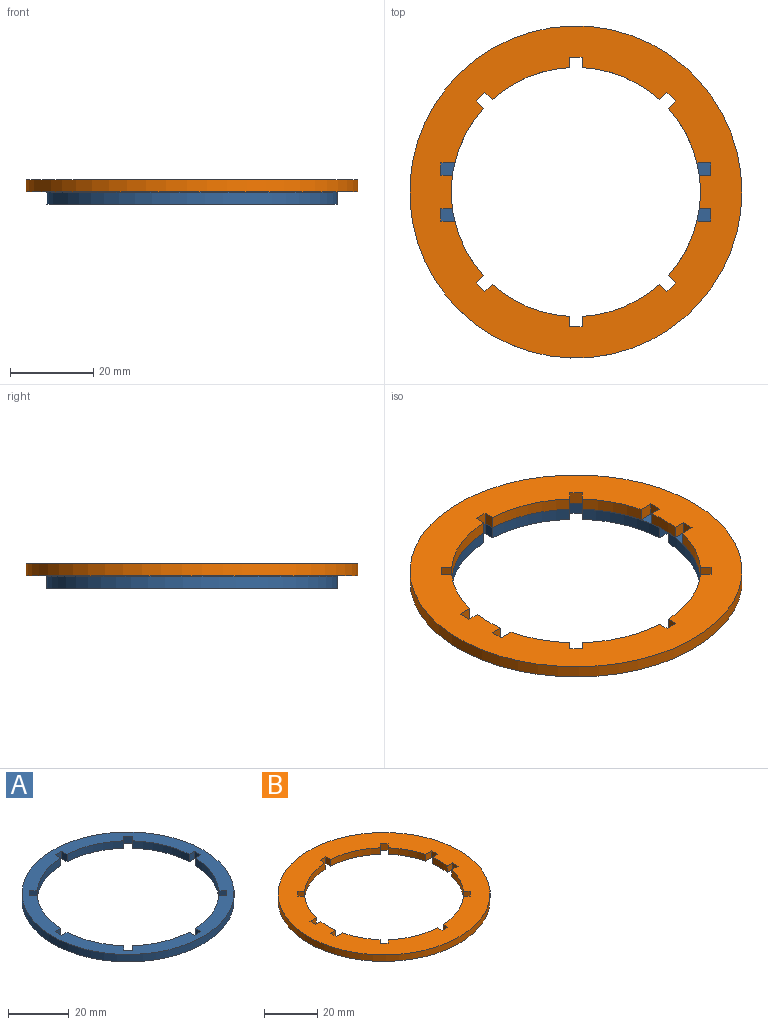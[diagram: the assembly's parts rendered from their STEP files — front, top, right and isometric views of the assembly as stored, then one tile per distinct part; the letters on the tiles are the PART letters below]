
ASSEMBLY  parts=2 mates=1
PART A: 35 faces, bbox 70x70x3 mm
  f0: cylinder r=30mm len=18.63mm, axis (0,0,-1), area 61.7mm2, adj f1,f31,f33,f34
  f1: plane 3x1.79mm, normal (-0.71,0.71,0), area 7.6mm2, adj f0,f2,f33,f34
  f2: plane 3x2.12mm, normal (0.71,0.71,0), area 9mm2, adj f1,f3,f33,f34
  f3: plane 3x1.79mm, normal (0.71,-0.71,0), area 7.6mm2, adj f2,f4,f33,f34
  f4: cylinder r=30mm len=18.63mm, axis (0,0,-1), area 61.7mm2, adj f3,f5,f33,f34
  f5: plane 3x2.54mm, normal (0,1,0), area 7.6mm2, adj f4,f6,f33,f34
  f6: plane 3x3mm, normal (1,0,0), area 9mm2, adj f5,f7,f33,f34
  f7: plane 3x2.54mm, normal (0,-1,0), area 7.6mm2, adj f6,f8,f33,f34
  f8: cylinder r=30mm len=18.63mm, axis (0,0,-1), area 61.7mm2, adj f7,f9,f33,f34
  f9: plane 3x1.79mm, normal (0.71,0.71,0), area 7.6mm2, adj f8,f10,f33,f34
  f10: plane 3x2.12mm, normal (0.71,-0.71,0), area 9mm2, adj f9,f11,f33,f34
  f11: plane 3x1.79mm, normal (-0.71,-0.71,0), area 7.6mm2, adj f10,f12,f33,f34
  f12: cylinder r=30mm len=18.63mm, axis (0,0,-1), area 61.7mm2, adj f11,f13,f33,f34
  f13: plane 3x2.54mm, normal (1,0,0), area 7.6mm2, adj f12,f14,f33,f34
  f14: plane 3x3mm, normal (0,-1,0), area 9mm2, adj f13,f15,f33,f34
  f15: plane 3x2.54mm, normal (-1,0,0), area 7.6mm2, adj f14,f16,f33,f34
  f16: cylinder r=30mm len=18.63mm, axis (0,0,-1), area 61.7mm2, adj f15,f17,f33,f34
  f17: plane 3x1.79mm, normal (0.71,-0.71,0), area 7.6mm2, adj f16,f18,f33,f34
  f18: plane 3x2.12mm, normal (-0.71,-0.71,0), area 9mm2, adj f17,f19,f33,f34
  f19: plane 3x1.79mm, normal (-0.71,0.71,0), area 7.6mm2, adj f18,f20,f33,f34
  f20: cylinder r=30mm len=18.63mm, axis (0,0,-1), area 61.7mm2, adj f19,f21,f33,f34
  f21: plane 3x2.54mm, normal (0,-1,0), area 7.6mm2, adj f20,f22,f33,f34
  f22: plane 3x3mm, normal (-1,0,0), area 9mm2, adj f21,f23,f33,f34
  f23: plane 3x2.54mm, normal (0,1,0), area 7.6mm2, adj f22,f24,f33,f34
  f24: cylinder r=30mm len=18.63mm, axis (0,0,-1), area 61.7mm2, adj f23,f25,f33,f34
  f25: plane 3x1.79mm, normal (-0.71,-0.71,0), area 7.6mm2, adj f24,f26,f33,f34
  f26: plane 3x2.12mm, normal (-0.71,0.71,0), area 9mm2, adj f25,f27,f33,f34
  f27: plane 3x1.79mm, normal (0.71,0.71,0), area 7.6mm2, adj f26,f28,f33,f34
  f28: cylinder r=30mm len=18.63mm, axis (0,0,-1), area 61.7mm2, adj f27,f29,f33,f34
  f29: plane 3x2.54mm, normal (-1,0,0), area 7.6mm2, adj f28,f30,f33,f34
  f30: plane 3x3mm, normal (0,1,0), area 9mm2, adj f29,f31,f33,f34
  f31: plane 3x2.54mm, normal (1,0,0), area 7.6mm2, adj f0,f30,f33,f34
  f32: cylinder r=35mm len=70mm, axis (0,0,-1), area 659.7mm2, adj f33,f34
  f33: plane 70x70mm, normal (0,0,1), area 960.7mm2, adj f0,f1,f2,f3,f4,f5,f6,f7
  f34: plane 70x70mm, normal (0,0,-1), area 960.7mm2, adj f0,f1,f2,f3,f4,f5,f6,f7
PART B: 43 faces, bbox 80x80x3 mm
  f0: plane 3x3mm, normal (0,-1,0), area 9mm2, adj f1,f40,f41,f42
  f1: plane 3x2.54mm, normal (-1,0,0), area 7.6mm2, adj f0,f2,f41,f42
  f2: cylinder r=30mm len=18.63mm, axis (0,0,-1), area 61.7mm2, adj f1,f3,f41,f42
  f3: plane 3x1.79mm, normal (0.71,-0.71,0), area 7.6mm2, adj f2,f4,f41,f42
  f4: plane 3x2.12mm, normal (-0.71,-0.71,0), area 9mm2, adj f3,f5,f41,f42
  f5: plane 3x1.79mm, normal (-0.71,0.71,0), area 7.6mm2, adj f4,f6,f41,f42
  f6: cylinder r=30mm len=13.13mm, axis (0,0,-1), area 45mm2, adj f5,f7,f41,f42
  f7: plane 3.33x3mm, normal (0,-1,0), area 10mm2, adj f6,f8,f41,f42
  f8: plane 3x3mm, normal (-1,0,0), area 9mm2, adj f7,f9,f41,f42
  f9: plane 3x2.77mm, normal (0,1,0), area 8.3mm2, adj f8,f10,f41,f42
  f10: cylinder r=30mm len=8mm, axis (0,0,-1), area 24.1mm2, adj f9,f11,f41,f42
  f11: plane 3x2.77mm, normal (0,-1,0), area 8.3mm2, adj f10,f12,f41,f42
  f12: plane 3x3mm, normal (-1,0,0), area 9mm2, adj f11,f13,f41,f42
  f13: plane 3.33x3mm, normal (0,1,0), area 10mm2, adj f12,f14,f41,f42
  f14: cylinder r=30mm len=13.13mm, axis (0,0,-1), area 45mm2, adj f13,f15,f41,f42
  f15: plane 3x1.79mm, normal (-0.71,-0.71,0), area 7.6mm2, adj f14,f16,f41,f42
  f16: plane 3x2.12mm, normal (-0.71,0.71,0), area 9mm2, adj f15,f17,f41,f42
  f17: plane 3x1.79mm, normal (0.71,0.71,0), area 7.6mm2, adj f16,f18,f41,f42
  f18: cylinder r=30mm len=18.63mm, axis (0,0,-1), area 61.7mm2, adj f17,f19,f41,f42
  f19: plane 3x2.54mm, normal (-1,0,0), area 7.6mm2, adj f18,f20,f41,f42
  f20: plane 3x3mm, normal (0,1,0), area 9mm2, adj f19,f21,f41,f42
  f21: plane 3x2.54mm, normal (1,0,0), area 7.6mm2, adj f20,f22,f41,f42
  f22: cylinder r=30mm len=18.63mm, axis (0,0,-1), area 61.7mm2, adj f21,f23,f41,f42
  f23: plane 3x1.79mm, normal (-0.71,0.71,0), area 7.6mm2, adj f22,f24,f41,f42
  f24: plane 3x2.12mm, normal (0.71,0.71,0), area 9mm2, adj f23,f25,f41,f42
  f25: plane 3x1.79mm, normal (0.71,-0.71,0), area 7.6mm2, adj f24,f26,f41,f42
  f26: cylinder r=30mm len=13.13mm, axis (0,0,-1), area 45mm2, adj f25,f27,f41,f42
  f27: plane 3.33x3mm, normal (0,1,0), area 10mm2, adj f26,f28,f41,f42
  f28: plane 3x3mm, normal (1,0,0), area 9mm2, adj f27,f29,f41,f42
  f29: plane 3x2.77mm, normal (0,-1,0), area 8.3mm2, adj f28,f30,f41,f42
  f30: cylinder r=30mm len=8mm, axis (0,0,-1), area 24.1mm2, adj f29,f31,f41,f42
  f31: plane 3x2.77mm, normal (0,1,0), area 8.3mm2, adj f30,f32,f41,f42
  f32: plane 3x3mm, normal (1,0,0), area 9mm2, adj f31,f33,f41,f42
  f33: plane 3.33x3mm, normal (0,-1,0), area 10mm2, adj f32,f34,f41,f42
  f34: cylinder r=30mm len=13.13mm, axis (0,0,-1), area 45mm2, adj f33,f35,f41,f42
  f35: plane 3x1.79mm, normal (0.71,0.71,0), area 7.6mm2, adj f34,f36,f41,f42
  f36: plane 3x2.12mm, normal (0.71,-0.71,0), area 9mm2, adj f35,f37,f41,f42
  f37: plane 3x1.79mm, normal (-0.71,-0.71,0), area 7.6mm2, adj f36,f38,f41,f42
  f38: cylinder r=30mm len=18.63mm, axis (0,0,-1), area 61.7mm2, adj f37,f40,f41,f42
  f39: cylinder r=40mm len=80mm, axis (0,0,-1), area 754mm2, adj f41,f42
  f40: plane 3x2.54mm, normal (1,0,0), area 7.6mm2, adj f0,f38,f41,f42
  f41: plane 80x80mm, normal (0,0,1), area 2117.6mm2, adj f0,f1,f2,f3,f4,f5,f6,f7
  f42: plane 80x80mm, normal (0,0,-1), area 2117.6mm2, adj f0,f1,f2,f3,f4,f5,f6,f7
PLACE A t=(0,0,34)mm
PLACE B at identity
MATE fastened A.f32 <-> B.f39  axis (0,0,1) through (0,0,-246)mm
